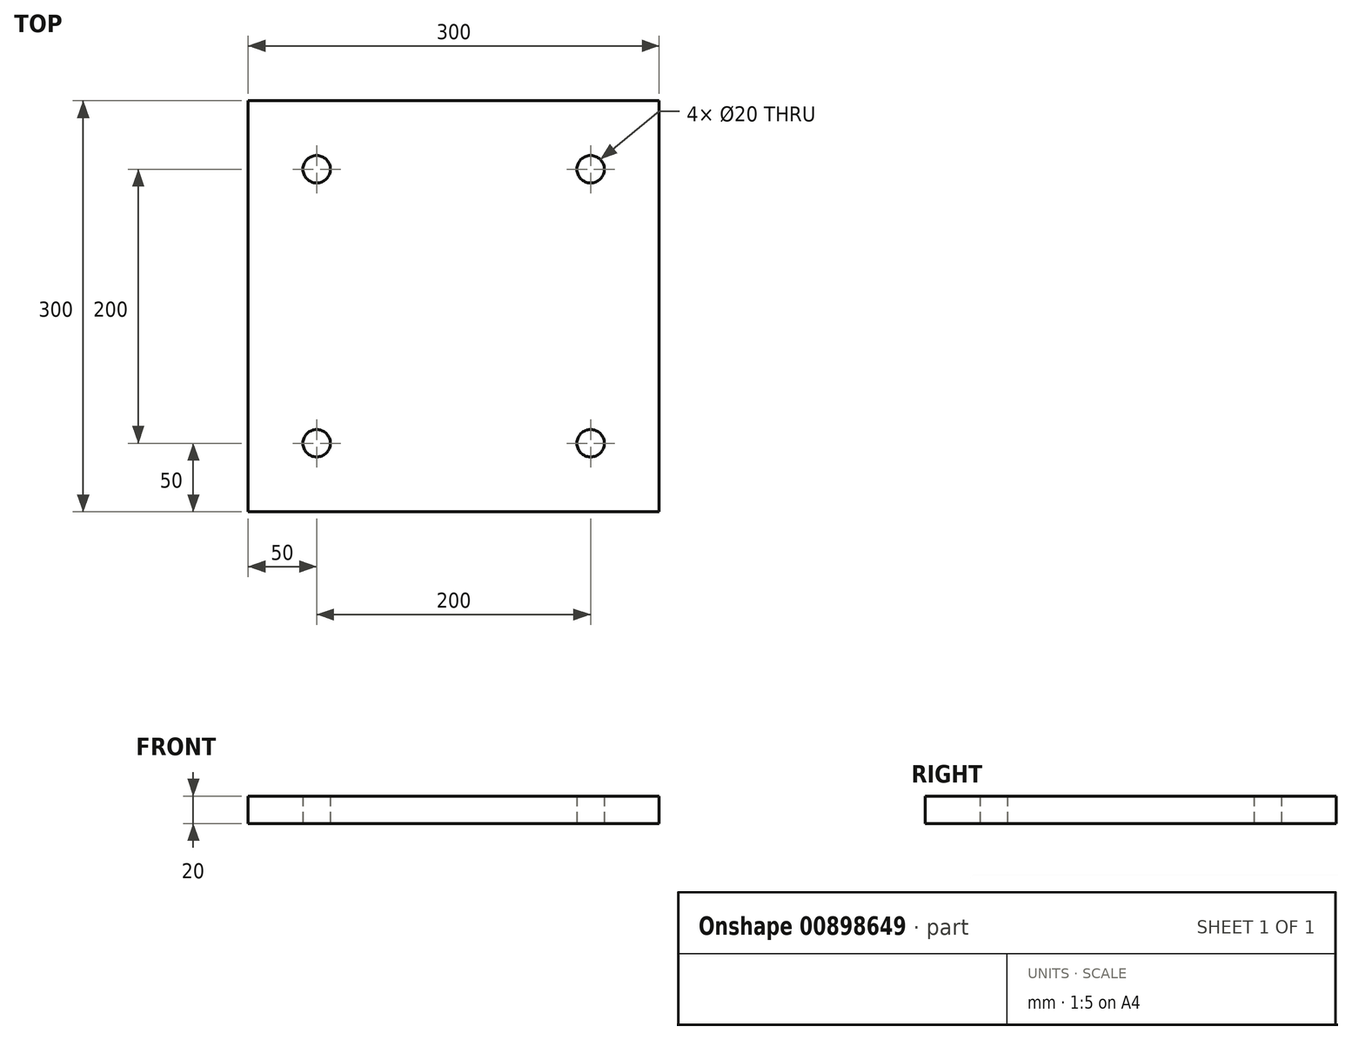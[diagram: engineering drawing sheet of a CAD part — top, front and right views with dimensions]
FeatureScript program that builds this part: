
annotation { "Feature Type Name" : "Feature", "Feature Type Description" : "" }
export const myFeature = defineFeature(function(context is Context, id is Id, definition is map)
    precondition{}
    {
        {
            var Q0;
            Q0=qCreatedBy(makeId("Top.planeOp"),FACE);
            var sketch = newSketch(context, id + "F0", { "sketchPlane" : qUnion([Q0])});
            skLineSegment(sketch, "E0.bottom", {"start": v(150, 150) * mm, "end": v(-150, 150) * mm});
            skLineSegment(sketch, "E0.top", {"start": v(150, -150) * mm, "end": v(-150, -150) * mm});
            skLineSegment(sketch, "E0.left", {"start": v(150, 150) * mm, "end": v(150, -150) * mm});
            skLineSegment(sketch, "E0.right", {"start": v(-150, 150) * mm, "end": v(-150, -150) * mm});
            skPoint(sketch, "E0.middle", {"position": v(0, 0) * mm});
            skCircle(sketch, "E1", {"center": v(-100, 100) * mm, "radius": 10 * mm});
            skCircle(sketch, "E2", {"center": v(100, 100) * mm, "radius": 10 * mm});
            skCircle(sketch, "E3", {"center": v(-100, -100) * mm, "radius": 10 * mm});
            skCircle(sketch, "E4", {"center": v(100, -100) * mm, "radius": 10 * mm});
            skSolve(sketch);
        }
        {
            var Q0;
            Q0=makeQuery(id+"F0.imprint","IMPRINT",FACE,{"disambiguationData":[TD([[makeQuery(id+"F0.imprint","IMPRINT",EDGE,{"derivedFrom":sQuery(id+"F0.wireOp",EDGE,"E0.bottom")}),1.0]])]});
            extrude(context, id + "F1", {"entities" : qUnion([Q0]), "depth" : 20 * mm, "offsetDistance" : 25 * mm});
        }
    });
